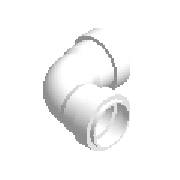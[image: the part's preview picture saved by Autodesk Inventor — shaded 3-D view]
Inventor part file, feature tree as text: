
AUTODESK INVENTOR PART (.ipt)
format: ipt  version: 2023.2 (Build 272271030, 271C)  size: 268,288 bytes
history: native  units: mm (DEFAULTED — no unit token found)
features: other x4, sketch x3, revolve x1
ambient origin geometry x8: Origin, YZ Plane, XZ Plane, XY Plane, X Axis, Y Axis, Z Axis, Center Point
bodies: Solid1 (feature_tree)
feature tree (8):
  sketch  "Sketch1"  dims[d3=90.0deg d0=2.25mm]
  revolve  "Revolution1"  [1 undecoded]
  sketch  "Sketch2"  dims[d1=2.25mm]
  other  "Work Axis31"
  other  "Work Point21"
  other  "Work Axis32"
  other  "Work Point22"
  sketch  "Sketch3"  dims[d2=2.25mm d4=2.7mm d5=2.25mm d6=6.75mm d7=40.3mm d8=18.0mm d9=18.0mm d10=0.0mm d11=6.3mm d12=40.0mm d13=3.0mm d14=2.7mm d15=32.0mm d16=32.0mm d17=40.3mm d18=2.25mm d19=2.25mm d20=2.25mm d21=2.25mm d22=4.5mm d23=2.7mm d24=3.0mm d25=40.0mm d26=6.3mm d27=18.0mm d28=18.0mm d29=32.0mm d30=32.0mm d31=2.7mm d206=90.0deg d207=0.0mm]
note: 1 required parameter value undecoded (feature->parameter linkage not recoverable at this tier; creation-order binding heuristic only, values carry confidence <= 0.55)
